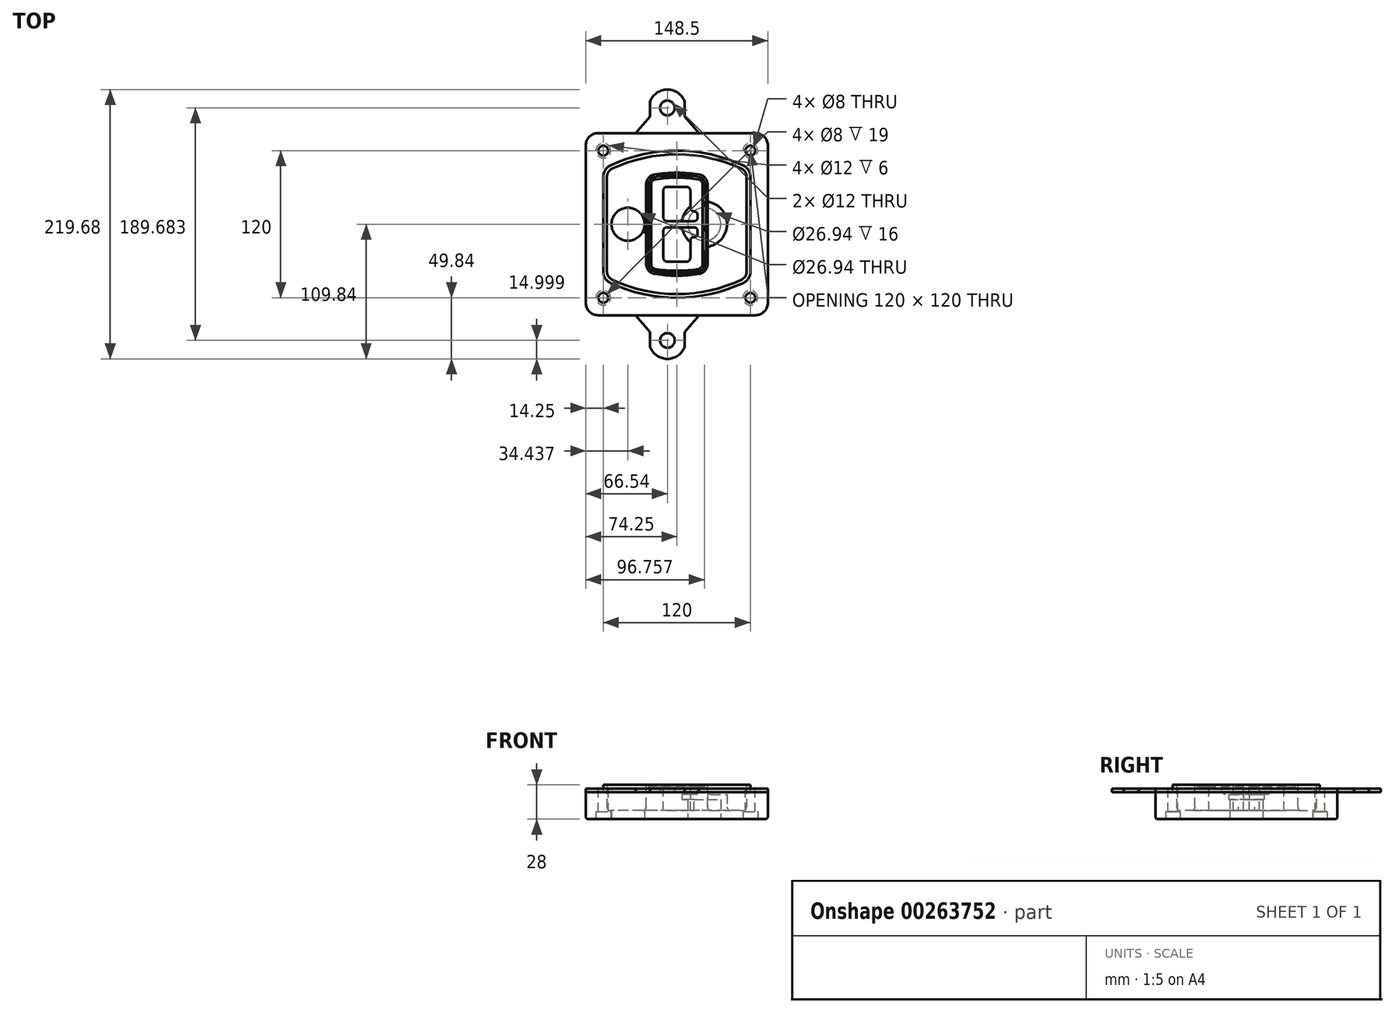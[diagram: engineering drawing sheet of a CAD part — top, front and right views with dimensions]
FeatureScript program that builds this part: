
annotation { "Feature Type Name" : "Feature", "Feature Type Description" : "" }
export const myFeature = defineFeature(function(context is Context, id is Id, definition is map)
    precondition{}
    {
        {
            var Q0;
            Q0=qCreatedBy(makeId("Top.planeOp"),FACE);
            var sketch = newSketch(context, id + "F0", { "sketchPlane" : qUnion([Q0])});
            skPoint(sketch, "E0.rect.middle", {"position": v(0, 0) * mm});
            skLineSegment(sketch, "E1.bottom", {"start": v(-64.25, -74.25) * mm, "end": v(64.25, -74.25) * mm});
            skLineSegment(sketch, "E1.top", {"start": v(-64.25, 74.25) * mm, "end": v(64.25, 74.25) * mm});
            skLineSegment(sketch, "E1.left", {"start": v(-74.25, -64.25) * mm, "end": v(-74.25, 64.25) * mm});
            skLineSegment(sketch, "E1.right", {"start": v(74.25, -64.25) * mm, "end": v(74.25, 64.25) * mm});
            skLineSegment(sketch, "E2", {"start": v(-74.25, 74.25) * mm, "end": v(74.25, -74.25) * mm, "construction": true});
            skLineSegment(sketch, "E3", {"start": v(74.25, 74.25) * mm, "end": v(-74.25, -74.25) * mm, "construction": true});
            skCircle(sketch, "E4", {"center": v(-60, 60) * mm, "radius": 4 * mm});
            skCircle(sketch, "E5", {"center": v(60, 60) * mm, "radius": 4 * mm});
            skCircle(sketch, "E6", {"center": v(60, -60) * mm, "radius": 4 * mm});
            skCircle(sketch, "E7", {"center": v(-60, -60) * mm, "radius": 4 * mm});
            skLineSegment(sketch, "E8", {"start": v(-60, 60) * mm, "end": v(60, 60) * mm, "construction": true});
            skLineSegment(sketch, "E9", {"start": v(60, 60) * mm, "end": v(60, -60) * mm, "construction": true});
            skLineSegment(sketch, "E10", {"start": v(60, -60) * mm, "end": v(-60, -60) * mm, "construction": true});
            skLineSegment(sketch, "E11", {"start": v(-60, -60) * mm, "end": v(-60, 60) * mm, "construction": true});
            skLineSegment(sketch, "E12", {"start": v(-60, 38.83) * mm, "end": v(-60, -38.83) * mm});
            skLineSegment(sketch, "E13", {"start": v(60, 38.83) * mm, "end": v(60, -38.83) * mm});
            skArc(sketch, "E14", {"start": v(54.26, 47.88) * mm, "mid": v(0, 60) * mm, "end": v(-54.26, 47.88) * mm});
            skArc(sketch, "E15", {"start": v(-54.26, -47.88) * mm, "mid": v(0, -60) * mm, "end": v(54.26, -47.88) * mm});
            skLineSegment(sketch, "E16", {"start": v(-60, 0) * mm, "end": v(60, 0) * mm, "construction": true});
            skPoint(sketch, "E17.visualSharp", {"position": v(-60, -45) * mm});
            skArc(sketch, "E17.filletArc", {"start": v(-60, -38.83) * mm, "mid": v(-58.44, -44.2) * mm, "end": v(-54.26, -47.88) * mm});
            skPoint(sketch, "E18.visualSharp", {"position": v(-60, 45) * mm});
            skArc(sketch, "E18.filletArc", {"start": v(-54.26, 47.88) * mm, "mid": v(-58.44, 44.2) * mm, "end": v(-60, 38.83) * mm});
            skPoint(sketch, "E19.visualSharp", {"position": v(60, 45) * mm});
            skArc(sketch, "E19.filletArc", {"start": v(60, 38.83) * mm, "mid": v(58.44, 44.2) * mm, "end": v(54.26, 47.88) * mm});
            skPoint(sketch, "E20.visualSharp", {"position": v(60, -45) * mm});
            skArc(sketch, "E20.filletArc", {"start": v(54.26, -47.88) * mm, "mid": v(58.44, -44.2) * mm, "end": v(60, -38.83) * mm});
            skPoint(sketch, "E21.visualSharp", {"position": v(-74.25, 74.25) * mm});
            skArc(sketch, "E21.filletArc", {"start": v(-64.25, 74.25) * mm, "mid": v(-71.32, 71.32) * mm, "end": v(-74.25, 64.25) * mm});
            skPoint(sketch, "E22.visualSharp", {"position": v(74.25, 74.25) * mm});
            skArc(sketch, "E22.filletArc", {"start": v(74.25, 64.25) * mm, "mid": v(71.32, 71.32) * mm, "end": v(64.25, 74.25) * mm});
            skPoint(sketch, "E23.visualSharp", {"position": v(74.25, -74.25) * mm});
            skArc(sketch, "E23.filletArc", {"start": v(64.25, -74.25) * mm, "mid": v(71.32, -71.32) * mm, "end": v(74.25, -64.25) * mm});
            skPoint(sketch, "E24.visualSharp", {"position": v(-74.25, -74.25) * mm});
            skArc(sketch, "E24.filletArc", {"start": v(-74.25, -64.25) * mm, "mid": v(-71.32, -71.32) * mm, "end": v(-64.25, -74.25) * mm});
            skArc(sketch, "E25.0", {"start": v(57, 38.83) * mm, "mid": v(55.9, 42.58) * mm, "end": v(52.98, 45.17) * mm});
            skLineSegment(sketch, "E25.1", {"start": v(57, 38.83) * mm, "end": v(57, -38.83) * mm});
            skArc(sketch, "E25.2", {"start": v(52.98, -45.17) * mm, "mid": v(55.9, -42.58) * mm, "end": v(57, -38.83) * mm});
            skArc(sketch, "E25.3", {"start": v(-52.98, -45.17) * mm, "mid": v(0, -57) * mm, "end": v(52.98, -45.17) * mm});
            skArc(sketch, "E25.4", {"start": v(-57, -38.83) * mm, "mid": v(-55.9, -42.58) * mm, "end": v(-52.98, -45.17) * mm});
            skArc(sketch, "E25.5", {"start": v(52.98, 45.17) * mm, "mid": v(0, 57) * mm, "end": v(-52.98, 45.17) * mm});
            skLineSegment(sketch, "E25.6", {"start": v(-57, 38.83) * mm, "end": v(-57, -38.83) * mm});
            skArc(sketch, "E25.7", {"start": v(-52.98, 45.17) * mm, "mid": v(-55.9, 42.58) * mm, "end": v(-57, 38.83) * mm});
            skArc(sketch, "E26.0", {"start": v(-55.96, 51.5) * mm, "mid": v(-61.82, 46.33) * mm, "end": v(-64, 38.83) * mm});
            skArc(sketch, "E26.1", {"start": v(55.96, 51.5) * mm, "mid": v(0, 64) * mm, "end": v(-55.96, 51.5) * mm});
            skArc(sketch, "E26.2", {"start": v(64, 38.83) * mm, "mid": v(61.82, 46.33) * mm, "end": v(55.96, 51.5) * mm});
            skLineSegment(sketch, "E26.3", {"start": v(64, 38.83) * mm, "end": v(64, -38.83) * mm});
            skArc(sketch, "E26.4", {"start": v(55.96, -51.5) * mm, "mid": v(61.82, -46.33) * mm, "end": v(64, -38.83) * mm});
            skLineSegment(sketch, "E26.5", {"start": v(-64, 38.83) * mm, "end": v(-64, -38.83) * mm});
            skArc(sketch, "E26.6", {"start": v(-55.96, -51.5) * mm, "mid": v(0, -64) * mm, "end": v(55.96, -51.5) * mm});
            skArc(sketch, "E26.7", {"start": v(-64, -38.83) * mm, "mid": v(-61.82, -46.33) * mm, "end": v(-55.96, -51.5) * mm});
            skSolve(sketch);
        }
        {
            var Q0;
            Q0=makeQuery(id+"F0.imprint","IMPRINT",FACE,{"disambiguationData":[TD([[makeQuery(id+"F0.imprint","IMPRINT",EDGE,{"derivedFrom":sQuery(id+"F0.wireOp",EDGE,"E1.bottom")}),1.0]])]});
            var Q1;
            Q1=makeQuery(id+"F0.imprint","IMPRINT",FACE,{"disambiguationData":[TD([[makeQuery(id+"F0.imprint","IMPRINT",EDGE,{"derivedFrom":sQuery(id+"F0.wireOp",EDGE,"E12")}),1.0]])]});
            var Q2;
            Q2=makeQuery(id+"F0.imprint","IMPRINT",FACE,{"disambiguationData":[TD([[makeQuery(id+"F0.imprint","IMPRINT",EDGE,{"derivedFrom":sQuery(id+"F0.wireOp",EDGE,"E25.0")}),1.0]])]});
            var Q3;
            Q3=makeQuery(id+"F0.imprint","IMPRINT",FACE,{"disambiguationData":[TD([[makeQuery(id+"F0.imprint","IMPRINT",EDGE,{"derivedFrom":sQuery(id+"F0.wireOp",EDGE,"E12")}),-1.0]])]});
            extrude(context, id + "F1", {"entities" : qUnion([Q0, Q1, Q2, Q3]), "oppositeDirection" : true, "depth" : 25 * mm});
        }
        {
            var Q0;
            Q0=makeQuery(id+"F0.imprint","IMPRINT",FACE,{"disambiguationData":[TD([[makeQuery(id+"F0.imprint","IMPRINT",EDGE,{"derivedFrom":sQuery(id+"F0.wireOp",EDGE,"E12")}),1.0]])]});
            extrude(context, id + "F2", {"entities" : qUnion([Q0]), "operationType" : NewBodyOperationType.ADD, "depth" : 3 * mm});
        }
        {
            var Q0;
            Q0=makeQuery(id+"F0.imprint","IMPRINT",FACE,{"disambiguationData":[TD([[makeQuery(id+"F0.imprint","IMPRINT",EDGE,{"derivedFrom":sQuery(id+"F0.wireOp",EDGE,"E25.0")}),1.0]])]});
            extrude(context, id + "F3", {"entities" : qUnion([Q0]), "operationType" : NewBodyOperationType.REMOVE, "oppositeDirection" : true, "depth" : 18 * mm});
        }
        {
            var Q0;
            Q0=makeQuery(id+"F2.opExtrude","CAP_FACE",FACE,{"disambiguationData":[OSD([sQuery(id+"F0.wireOp",EDGE,"E12"),sQuery(id+"F0.wireOp",EDGE,"E13"),sQuery(id+"F0.wireOp",EDGE,"E14"),sQuery(id+"F0.wireOp",EDGE,"E15"),sQuery(id+"F0.wireOp",EDGE,"E17.filletArc"),sQuery(id+"F0.wireOp",EDGE,"E18.filletArc"),sQuery(id+"F0.wireOp",EDGE,"E19.filletArc"),sQuery(id+"F0.wireOp",EDGE,"E20.filletArc"),sQuery(id+"F0.wireOp",EDGE,"E25.0"),sQuery(id+"F0.wireOp",EDGE,"E25.1"),sQuery(id+"F0.wireOp",EDGE,"E25.2"),sQuery(id+"F0.wireOp",EDGE,"E25.3"),sQuery(id+"F0.wireOp",EDGE,"E25.4"),sQuery(id+"F0.wireOp",EDGE,"E25.5"),sQuery(id+"F0.wireOp",EDGE,"E25.6"),sQuery(id+"F0.wireOp",EDGE,"E25.7")])],"isStart":false});
            var sketch = newSketch(context, id + "F4", { "sketchPlane" : qUnion([Q0])});
            skArc(sketch, "E27.0", {"start": v(-18.34, -40.45) * mm, "mid": v(0, -42) * mm, "end": v(18.34, -40.45) * mm});
            skArc(sketch, "E28.0", {"start": v(18.34, 40.45) * mm, "mid": v(0, 42) * mm, "end": v(-18.34, 40.45) * mm});
            skLineSegment(sketch, "E29", {"start": v(-25, 32.57) * mm, "end": v(-25, -32.57) * mm});
            skLineSegment(sketch, "E30", {"start": v(25, 32.57) * mm, "end": v(25, -32.57) * mm});
            skLineSegment(sketch, "E31", {"start": v(-25, 39.1) * mm, "end": v(25, 39.1) * mm, "construction": true});
            skLineSegment(sketch, "E32", {"start": v(-25, -39.1) * mm, "end": v(25, -39.1) * mm, "construction": true});
            skPoint(sketch, "E33.visualSharp", {"position": v(-25, 39.1) * mm});
            skArc(sketch, "E33.filletArc", {"start": v(-18.34, 40.45) * mm, "mid": v(-23.11, 37.73) * mm, "end": v(-25, 32.57) * mm});
            skPoint(sketch, "E34.visualSharp", {"position": v(25, 39.1) * mm});
            skArc(sketch, "E34.filletArc", {"start": v(25, 32.57) * mm, "mid": v(23.11, 37.73) * mm, "end": v(18.34, 40.45) * mm});
            skPoint(sketch, "E35.visualSharp", {"position": v(25, -39.1) * mm});
            skArc(sketch, "E35.filletArc", {"start": v(18.34, -40.45) * mm, "mid": v(23.11, -37.73) * mm, "end": v(25, -32.57) * mm});
            skPoint(sketch, "E36.visualSharp", {"position": v(-25, -39.1) * mm});
            skArc(sketch, "E36.filletArc", {"start": v(-25, -32.57) * mm, "mid": v(-23.11, -37.73) * mm, "end": v(-18.34, -40.45) * mm});
            skArc(sketch, "E37.0", {"start": v(52.98, 45.17) * mm, "mid": v(0, 57) * mm, "end": v(-52.98, 45.17) * mm});
            skArc(sketch, "E37.1", {"start": v(-52.98, 45.17) * mm, "mid": v(-55.9, 42.58) * mm, "end": v(-57, 38.83) * mm});
            skLineSegment(sketch, "E37.2", {"start": v(-57, 38.83) * mm, "end": v(-57, -38.83) * mm});
            skArc(sketch, "E37.3", {"start": v(-57, -38.83) * mm, "mid": v(-55.9, -42.58) * mm, "end": v(-52.98, -45.17) * mm});
            skArc(sketch, "E37.4", {"start": v(-52.98, -45.17) * mm, "mid": v(0, -57) * mm, "end": v(52.98, -45.17) * mm});
            skArc(sketch, "E37.5", {"start": v(52.98, -45.17) * mm, "mid": v(55.9, -42.58) * mm, "end": v(57, -38.83) * mm});
            skLineSegment(sketch, "E37.6", {"start": v(57, 38.83) * mm, "end": v(57, -38.83) * mm});
            skArc(sketch, "E37.7", {"start": v(57, 38.83) * mm, "mid": v(55.9, 42.58) * mm, "end": v(52.98, 45.17) * mm});
            skLineSegment(sketch, "E38.0", {"start": v(23, 32.57) * mm, "end": v(23, -32.57) * mm});
            skArc(sketch, "E38.1", {"start": v(18, -38.48) * mm, "mid": v(21.58, -36.44) * mm, "end": v(23, -32.57) * mm});
            skArc(sketch, "E38.2", {"start": v(-18, -38.48) * mm, "mid": v(0, -40) * mm, "end": v(18, -38.48) * mm});
            skArc(sketch, "E38.3", {"start": v(-23, -32.57) * mm, "mid": v(-21.58, -36.44) * mm, "end": v(-18, -38.48) * mm});
            skLineSegment(sketch, "E38.4", {"start": v(-23, 32.57) * mm, "end": v(-23, -32.57) * mm});
            skArc(sketch, "E38.5", {"start": v(23, 32.57) * mm, "mid": v(21.58, 36.44) * mm, "end": v(18, 38.48) * mm});
            skArc(sketch, "E38.6", {"start": v(-18, 38.48) * mm, "mid": v(-21.58, 36.44) * mm, "end": v(-23, 32.57) * mm});
            skArc(sketch, "E38.7", {"start": v(18, 38.48) * mm, "mid": v(0, 40) * mm, "end": v(-18, 38.48) * mm});
            skArc(sketch, "E39.0", {"start": v(21, 32.57) * mm, "mid": v(20.06, 35.15) * mm, "end": v(17.67, 36.5) * mm});
            skLineSegment(sketch, "E39.1", {"start": v(21, 32.57) * mm, "end": v(21, -32.57) * mm});
            skArc(sketch, "E39.2", {"start": v(17.67, -36.5) * mm, "mid": v(20.06, -35.15) * mm, "end": v(21, -32.57) * mm});
            skArc(sketch, "E39.3", {"start": v(-17.67, -36.5) * mm, "mid": v(0, -38) * mm, "end": v(17.67, -36.5) * mm});
            skArc(sketch, "E39.4", {"start": v(-21, -32.57) * mm, "mid": v(-20.06, -35.15) * mm, "end": v(-17.67, -36.5) * mm});
            skArc(sketch, "E39.5", {"start": v(17.67, 36.5) * mm, "mid": v(0, 38) * mm, "end": v(-17.67, 36.5) * mm});
            skLineSegment(sketch, "E39.6", {"start": v(-21, 32.57) * mm, "end": v(-21, -32.57) * mm});
            skArc(sketch, "E39.7", {"start": v(-17.67, 36.5) * mm, "mid": v(-20.06, 35.15) * mm, "end": v(-21, 32.57) * mm});
            skLineSegment(sketch, "E40", {"start": v(-25, 0) * mm, "end": v(25, 0) * mm, "construction": true});
            skLineSegment(sketch, "E41", {"start": v(-11, 5.5) * mm, "end": v(-11, 27.5) * mm});
            skLineSegment(sketch, "E42", {"start": v(-8, 30.5) * mm, "end": v(8, 30.5) * mm});
            skLineSegment(sketch, "E43", {"start": v(11, 27.5) * mm, "end": v(11, 13.5) * mm});
            skLineSegment(sketch, "E44", {"start": v(14, 10.5) * mm, "end": v(14, 10.5) * mm});
            skLineSegment(sketch, "E45", {"start": v(17, 7.5) * mm, "end": v(17, 5.5) * mm});
            skLineSegment(sketch, "E46", {"start": v(14, 2.5) * mm, "end": v(-8, 2.5) * mm});
            skPoint(sketch, "E47.visualSharp", {"position": v(-11, 30.5) * mm});
            skArc(sketch, "E47.filletArc", {"start": v(-8, 30.5) * mm, "mid": v(-10.12, 29.62) * mm, "end": v(-11, 27.5) * mm});
            skPoint(sketch, "E48.visualSharp", {"position": v(11, 30.5) * mm});
            skArc(sketch, "E48.filletArc", {"start": v(11, 27.5) * mm, "mid": v(10.12, 29.62) * mm, "end": v(8, 30.5) * mm});
            skPoint(sketch, "E49.visualSharp", {"position": v(11, 10.5) * mm});
            skArc(sketch, "E49.filletArc", {"start": v(11, 13.5) * mm, "mid": v(11.88, 11.38) * mm, "end": v(14, 10.5) * mm});
            skPoint(sketch, "E50.visualSharp", {"position": v(17, 10.5) * mm});
            skArc(sketch, "E50.filletArc", {"start": v(17, 7.5) * mm, "mid": v(16.12, 9.62) * mm, "end": v(14, 10.5) * mm});
            skPoint(sketch, "E51.visualSharp", {"position": v(17, 2.5) * mm});
            skArc(sketch, "E51.filletArc", {"start": v(14, 2.5) * mm, "mid": v(16.12, 3.38) * mm, "end": v(17, 5.5) * mm});
            skPoint(sketch, "E52.visualSharp", {"position": v(-11, 2.5) * mm});
            skArc(sketch, "E52.filletArc", {"start": v(-11, 5.5) * mm, "mid": v(-10.12, 3.38) * mm, "end": v(-8, 2.5) * mm});
            skLineSegment(sketch, "E53.0.MirrorCS", {"start": v(14, -2.5) * mm, "end": v(-8, -2.5) * mm});
            skArc(sketch, "E54.0.MirrorCS", {"start": v(-11, -5.5) * mm, "mid": v(-10.12, -3.38) * mm, "end": v(-8, -2.5) * mm});
            skLineSegment(sketch, "E55.0.MirrorCS", {"start": v(-11, -5.5) * mm, "end": v(-11, -27.5) * mm});
            skArc(sketch, "E56.0.MirrorCS", {"start": v(-8, -30.5) * mm, "mid": v(-10.12, -29.62) * mm, "end": v(-11, -27.5) * mm});
            skLineSegment(sketch, "E57.0.MirrorCS", {"start": v(-8, -30.5) * mm, "end": v(8, -30.5) * mm});
            skArc(sketch, "E58.0.MirrorCS", {"start": v(11, -27.5) * mm, "mid": v(10.12, -29.62) * mm, "end": v(8, -30.5) * mm});
            skLineSegment(sketch, "E59.0.MirrorCS", {"start": v(11, -27.5) * mm, "end": v(11, -13.5) * mm});
            skArc(sketch, "E60.0.MirrorCS", {"start": v(11, -13.5) * mm, "mid": v(11.88, -11.38) * mm, "end": v(14, -10.5) * mm});
            skArc(sketch, "E61.0.MirrorCS", {"start": v(17, -7.5) * mm, "mid": v(16.12, -9.62) * mm, "end": v(14, -10.5) * mm});
            skLineSegment(sketch, "E62.0.MirrorCS", {"start": v(17, -7.5) * mm, "end": v(17, -5.5) * mm});
            skArc(sketch, "E63.0.MirrorCS", {"start": v(14, -2.5) * mm, "mid": v(16.12, -3.38) * mm, "end": v(17, -5.5) * mm});
            skSolve(sketch);
        }
        {
            var Q0;
            Q0=makeQuery(id+"F4.imprint","IMPRINT",FACE,{"disambiguationData":[TD([[makeQuery(id+"F4.imprint","IMPRINT",EDGE,{"derivedFrom":sQuery(id+"F4.wireOp",EDGE,"E27.0")}),1.0]])]});
            var Q1;
            Q1=makeQuery(id+"F4.imprint","IMPRINT",FACE,{"disambiguationData":[TD([[makeQuery(id+"F4.imprint","IMPRINT",EDGE,{"derivedFrom":sQuery(id+"F4.wireOp",EDGE,"E38.0")}),-1.0]])]});
            var Q2;
            Q2=makeQuery(id+"F4.imprint","IMPRINT",FACE,{"disambiguationData":[TD([[makeQuery(id+"F4.imprint","IMPRINT",EDGE,{"derivedFrom":sQuery(id+"F4.wireOp",EDGE,"E39.0")}),1.0]])]});
            extrude(context, id + "F5", {"entities" : qUnion([Q0, Q1, Q2]), "operationType" : NewBodyOperationType.ADD, "endBound" : BoundingType.UP_TO_NEXT, "oppositeDirection" : true, "depth" : 25 * mm});
        }
        {
            var Q0;
            Q0=makeQuery(id+"F4.imprint","IMPRINT",FACE,{"disambiguationData":[TD([[makeQuery(id+"F4.imprint","IMPRINT",EDGE,{"derivedFrom":sQuery(id+"F4.wireOp",EDGE,"E38.0")}),-1.0]])]});
            extrude(context, id + "F6", {"entities" : qUnion([Q0]), "operationType" : NewBodyOperationType.REMOVE, "oppositeDirection" : true, "depth" : 2 * mm});
        }
        {
            var Q0;
            Q0=makeQuery(id+"F1.opExtrude","CAP_FACE",FACE,{"disambiguationData":[OSD([sQuery(id+"F0.wireOp",EDGE,"E1.bottom"),sQuery(id+"F0.wireOp",EDGE,"E1.top"),sQuery(id+"F0.wireOp",EDGE,"E1.left"),sQuery(id+"F0.wireOp",EDGE,"E1.right"),sQuery(id+"F0.wireOp",EDGE,"E4"),sQuery(id+"F0.wireOp",EDGE,"E5"),sQuery(id+"F0.wireOp",EDGE,"E6"),sQuery(id+"F0.wireOp",EDGE,"E7"),sQuery(id+"F0.wireOp",EDGE,"E21.filletArc"),sQuery(id+"F0.wireOp",EDGE,"E22.filletArc"),sQuery(id+"F0.wireOp",EDGE,"E23.filletArc"),sQuery(id+"F0.wireOp",EDGE,"E24.filletArc")])],"isStart":false});
            var sketch = newSketch(context, id + "F7", { "sketchPlane" : qUnion([Q0])});
            skCircle(sketch, "E64", {"center": v(22.5, 0) * mm, "radius": 13.47 * mm});
            skCircle(sketch, "E65", {"center": v(-39.81, 0) * mm, "radius": 13.47 * mm});
            skLineSegment(sketch, "E66", {"start": v(74.25, 0) * mm, "end": v(-74.25, 0) * mm});
            skCircle(sketch, "E67", {"center": v(22.5, 0) * mm, "radius": 18.47 * mm});
            skCircle(sketch, "E68", {"center": v(60, -60) * mm, "radius": 6 * mm});
            skCircle(sketch, "E69", {"center": v(-60, -60) * mm, "radius": 6 * mm});
            skCircle(sketch, "E70", {"center": v(-60, 60) * mm, "radius": 6 * mm});
            skCircle(sketch, "E71", {"center": v(60, 60) * mm, "radius": 6 * mm});
            skSolve(sketch);
        }
        {
            var Q0;
            {var subQ1=sQuery(id+"F7.wireOp",EDGE,"E66");var subQ4=sQuery(id+"F7.wireOp",EDGE,"E64");var subQ6=makeQuery(id+"F7.imprint","INTERSECT",VERTEX,{"disambiguationData":[OD(0.0)],"derivedFrom":[subQ4,subQ1]});Q0=makeQuery(id+"F7.imprint","IMPRINT",FACE,{"disambiguationData":[TD([[makeQuery(id+"F7.imprint","IMPRINT",EDGE,{"disambiguationData":[TD([[subQ6,-1.0]])],"derivedFrom":subQ4}),-1.0]])]});}
            var Q1;
            {var subQ0=sQuery(id+"F7.wireOp",EDGE,"E66");var subQ1=sQuery(id+"F7.wireOp",EDGE,"E64");var subQ3=makeQuery(id+"F7.imprint","INTERSECT",VERTEX,{"disambiguationData":[OD(0.0)],"derivedFrom":[subQ1,subQ0]});Q1=makeQuery(id+"F7.imprint","IMPRINT",FACE,{"disambiguationData":[TD([[makeQuery(id+"F7.imprint","IMPRINT",EDGE,{"disambiguationData":[TD([[subQ3,-1.0]])],"derivedFrom":subQ1}),1.0]])]});}
            var Q2;
            {var subQ0=sQuery(id+"F7.wireOp",EDGE,"E66");var subQ1=sQuery(id+"F7.wireOp",EDGE,"E64");var subQ3=makeQuery(id+"F7.imprint","INTERSECT",VERTEX,{"disambiguationData":[OD(0.0)],"derivedFrom":[subQ1,subQ0]});Q2=makeQuery(id+"F7.imprint","IMPRINT",FACE,{"disambiguationData":[TD([[makeQuery(id+"F7.imprint","IMPRINT",EDGE,{"disambiguationData":[TD([[subQ3,1.0]])],"derivedFrom":subQ1}),1.0]])]});}
            var Q3;
            {var subQ1=sQuery(id+"F7.wireOp",EDGE,"E66");var subQ4=sQuery(id+"F7.wireOp",EDGE,"E64");var subQ6=makeQuery(id+"F7.imprint","INTERSECT",VERTEX,{"disambiguationData":[OD(0.0)],"derivedFrom":[subQ4,subQ1]});Q3=makeQuery(id+"F7.imprint","IMPRINT",FACE,{"disambiguationData":[TD([[makeQuery(id+"F7.imprint","IMPRINT",EDGE,{"disambiguationData":[TD([[subQ6,1.0]])],"derivedFrom":subQ4}),-1.0]])]});}
            extrude(context, id + "F8", {"entities" : qUnion([Q0, Q1, Q2, Q3]), "operationType" : NewBodyOperationType.ADD, "oppositeDirection" : true, "depth" : 20 * mm});
        }
        {
            var Q0;
            {var subQ0=sQuery(id+"F7.wireOp",EDGE,"E66");var subQ1=sQuery(id+"F7.wireOp",EDGE,"E64");var subQ3=makeQuery(id+"F7.imprint","INTERSECT",VERTEX,{"disambiguationData":[OD(0.0)],"derivedFrom":[subQ1,subQ0]});Q0=makeQuery(id+"F7.imprint","IMPRINT",FACE,{"disambiguationData":[TD([[makeQuery(id+"F7.imprint","IMPRINT",EDGE,{"disambiguationData":[TD([[subQ3,-1.0]])],"derivedFrom":subQ1}),1.0]])]});}
            var Q1;
            {var subQ0=sQuery(id+"F7.wireOp",EDGE,"E66");var subQ1=sQuery(id+"F7.wireOp",EDGE,"E64");var subQ3=makeQuery(id+"F7.imprint","INTERSECT",VERTEX,{"disambiguationData":[OD(0.0)],"derivedFrom":[subQ1,subQ0]});Q1=makeQuery(id+"F7.imprint","IMPRINT",FACE,{"disambiguationData":[TD([[makeQuery(id+"F7.imprint","IMPRINT",EDGE,{"disambiguationData":[TD([[subQ3,1.0]])],"derivedFrom":subQ1}),1.0]])]});}
            extrude(context, id + "F9", {"entities" : qUnion([Q0, Q1]), "operationType" : NewBodyOperationType.REMOVE, "oppositeDirection" : true, "depth" : 16 * mm});
        }
        {
            var Q0;
            {var subQ0=sQuery(id+"F7.wireOp",EDGE,"E66");var subQ1=sQuery(id+"F7.wireOp",EDGE,"E65");var subQ3=makeQuery(id+"F7.imprint","INTERSECT",VERTEX,{"disambiguationData":[OD(0.0)],"derivedFrom":[subQ1,subQ0]});Q0=makeQuery(id+"F7.imprint","IMPRINT",FACE,{"disambiguationData":[TD([[makeQuery(id+"F7.imprint","IMPRINT",EDGE,{"disambiguationData":[TD([[subQ3,-1.0]])],"derivedFrom":subQ1}),1.0]])]});}
            var Q1;
            {var subQ0=sQuery(id+"F7.wireOp",EDGE,"E66");var subQ1=sQuery(id+"F7.wireOp",EDGE,"E65");var subQ3=makeQuery(id+"F7.imprint","INTERSECT",VERTEX,{"disambiguationData":[OD(0.0)],"derivedFrom":[subQ1,subQ0]});Q1=makeQuery(id+"F7.imprint","IMPRINT",FACE,{"disambiguationData":[TD([[makeQuery(id+"F7.imprint","IMPRINT",EDGE,{"disambiguationData":[TD([[subQ3,1.0]])],"derivedFrom":subQ1}),1.0]])]});}
            extrude(context, id + "F10", {"entities" : qUnion([Q0, Q1]), "operationType" : NewBodyOperationType.REMOVE, "oppositeDirection" : true, "depth" : 25 * mm});
        }
        {
            var Q0;
            Q0=makeQuery(id+"F7.imprint","IMPRINT",FACE,{"disambiguationData":[TD([[makeQuery(id+"F7.imprint","IMPRINT",EDGE,{"derivedFrom":sQuery(id+"F7.wireOp",EDGE,"E68")}),1.0]])]});
            var Q1;
            Q1=makeQuery(id+"F7.imprint","IMPRINT",FACE,{"disambiguationData":[TD([[makeQuery(id+"F7.imprint","IMPRINT",EDGE,{"derivedFrom":makeQuery(id+"F1.opExtrude","CAP_EDGE",EDGE,{"disambiguationData":[OSD([sQuery(id+"F0.wireOp",EDGE,"E5")])],"isStart":false})}),-1.0]])]});
            var Q2;
            Q2=makeQuery(id+"F7.imprint","IMPRINT",FACE,{"disambiguationData":[TD([[makeQuery(id+"F7.imprint","IMPRINT",EDGE,{"derivedFrom":sQuery(id+"F7.wireOp",EDGE,"E69")}),1.0]])]});
            var Q3;
            Q3=makeQuery(id+"F7.imprint","IMPRINT",FACE,{"disambiguationData":[TD([[makeQuery(id+"F7.imprint","IMPRINT",EDGE,{"derivedFrom":makeQuery(id+"F1.opExtrude","CAP_EDGE",EDGE,{"disambiguationData":[OSD([sQuery(id+"F0.wireOp",EDGE,"E4")])],"isStart":false})}),-1.0]])]});
            var Q4;
            Q4=makeQuery(id+"F7.imprint","IMPRINT",FACE,{"disambiguationData":[TD([[makeQuery(id+"F7.imprint","IMPRINT",EDGE,{"derivedFrom":sQuery(id+"F7.wireOp",EDGE,"E70")}),1.0]])]});
            var Q5;
            Q5=makeQuery(id+"F7.imprint","IMPRINT",FACE,{"disambiguationData":[TD([[makeQuery(id+"F7.imprint","IMPRINT",EDGE,{"derivedFrom":makeQuery(id+"F1.opExtrude","CAP_EDGE",EDGE,{"disambiguationData":[OSD([sQuery(id+"F0.wireOp",EDGE,"E7")])],"isStart":false})}),-1.0]])]});
            var Q6;
            Q6=makeQuery(id+"F7.imprint","IMPRINT",FACE,{"disambiguationData":[TD([[makeQuery(id+"F7.imprint","IMPRINT",EDGE,{"derivedFrom":sQuery(id+"F7.wireOp",EDGE,"E71")}),1.0]])]});
            var Q7;
            Q7=makeQuery(id+"F7.imprint","IMPRINT",FACE,{"disambiguationData":[TD([[makeQuery(id+"F7.imprint","IMPRINT",EDGE,{"derivedFrom":makeQuery(id+"F1.opExtrude","CAP_EDGE",EDGE,{"disambiguationData":[OSD([sQuery(id+"F0.wireOp",EDGE,"E6")])],"isStart":false})}),-1.0]])]});
            extrude(context, id + "F11", {"entities" : qUnion([Q0, Q1, Q2, Q3, Q4, Q5, Q6, Q7]), "operationType" : NewBodyOperationType.REMOVE, "oppositeDirection" : true, "depth" : 6 * mm});
        }
        {
            var Q0;
            Q0=makeQuery(id+"F9.boolean.opBoolean","COPY",FACE,{"derivedFrom":makeQuery(id+"F9.opExtrude","CAP_FACE",FACE,{"disambiguationData":[OSD([sQuery(id+"F7.wireOp",EDGE,"E64")])],"isStart":false})});
            var sketch = newSketch(context, id + "F12", { "sketchPlane" : qUnion([Q0])});
            skArc(sketch, "E72.0", {"start": v(11, 14.45) * mm, "mid": v(6.45, 9.13) * mm, "end": v(4.2, 2.5) * mm});
            skArc(sketch, "E72.1", {"start": v(4.2, -2.5) * mm, "mid": v(6.45, -9.13) * mm, "end": v(11, -14.45) * mm});
            skLineSegment(sketch, "E73", {"start": v(4.2, -2.5) * mm, "end": v(14, -2.5) * mm});
            skLineSegment(sketch, "E74.0", {"start": v(14, 2.5) * mm, "end": v(4.2, 2.5) * mm});
            skArc(sketch, "E74.1", {"start": v(14, 2.5) * mm, "mid": v(16.12, 3.38) * mm, "end": v(17, 5.5) * mm});
            skLineSegment(sketch, "E74.2", {"start": v(17, 7.5) * mm, "end": v(17, 5.5) * mm});
            skArc(sketch, "E74.3", {"start": v(17, 7.5) * mm, "mid": v(16.12, 9.62) * mm, "end": v(14, 10.5) * mm});
            skArc(sketch, "E74.4", {"start": v(11, 13.5) * mm, "mid": v(11.88, 11.38) * mm, "end": v(14, 10.5) * mm});
            skLineSegment(sketch, "E74.5", {"start": v(11, 14.45) * mm, "end": v(11, 13.5) * mm});
            skLineSegment(sketch, "E74.7", {"start": v(14, -2.5) * mm, "end": v(4.2, -2.5) * mm});
            skArc(sketch, "E74.8", {"start": v(14, -2.5) * mm, "mid": v(16.12, -3.38) * mm, "end": v(17, -5.5) * mm});
            skLineSegment(sketch, "E74.9", {"start": v(17, -7.5) * mm, "end": v(17, -5.5) * mm});
            skArc(sketch, "E74.10", {"start": v(17, -7.5) * mm, "mid": v(16.12, -9.62) * mm, "end": v(14, -10.5) * mm});
            skArc(sketch, "E74.11", {"start": v(11, -13.5) * mm, "mid": v(11.88, -11.38) * mm, "end": v(14, -10.5) * mm});
            skLineSegment(sketch, "E74.12", {"start": v(11, -14.45) * mm, "end": v(11, -13.5) * mm});
            skPoint(sketch, "E75.orphan", {"position": v(11, -27.5) * mm});
            skPoint(sketch, "E76.orphan", {"position": v(-8, -2.5) * mm});
            skPoint(sketch, "E77.orphan", {"position": v(-8, 2.5) * mm});
            skPoint(sketch, "E78.orphan", {"position": v(11, 27.5) * mm});
            skSolve(sketch);
        }
        {
            var Q0;
            {var subQ7=sQuery(id+"F12.wireOp",EDGE,"E72.0");var subQ14=sQuery(id+"F12.wireOp",EDGE,"E72.1");var subQ16=sQuery(id+"F12.wireOp",EDGE,"E74.1");var subQ18=sQuery(id+"F12.wireOp",EDGE,"E74.8");Q0=qUnion([makeQuery(id+"F12.imprint","IMPRINT",FACE,{"disambiguationData":[TD([[makeQuery(id+"F12.imprint","IMPRINT",EDGE,{"derivedFrom":subQ7}),1.0]])]}),makeQuery(id+"F12.imprint","IMPRINT",FACE,{"disambiguationData":[TD([[makeQuery(id+"F12.imprint","IMPRINT",EDGE,{"derivedFrom":subQ14}),1.0]])]}),makeQuery(id+"F12.imprint","IMPRINT",FACE,{"disambiguationData":[TD([[makeQuery(id+"F12.imprint","IMPRINT",EDGE,{"derivedFrom":subQ16}),1.0]])]}),makeQuery(id+"F12.imprint","IMPRINT",FACE,{"disambiguationData":[TD([[makeQuery(id+"F12.imprint","IMPRINT",EDGE,{"derivedFrom":subQ18}),-1.0]])]})]);}
            var Q1;
            Q1=makeQuery(id+"F5.boolean.opBoolean","SPLIT",FACE,{"disambiguationData":[TD([makeQuery(id+"F5.opExtrude","SWEPT_FACE",FACE,{"disambiguationData":[OSD([sQuery(id+"F4.wireOp",EDGE,"E41")])]})])],"derivedFrom":makeQuery(id+"F3.boolean.opBoolean","COPY",FACE,{"derivedFrom":makeQuery(id+"F3.opExtrude","CAP_FACE",FACE,{"disambiguationData":[OSD([sQuery(id+"F0.wireOp",EDGE,"E25.0"),sQuery(id+"F0.wireOp",EDGE,"E25.1"),sQuery(id+"F0.wireOp",EDGE,"E25.2"),sQuery(id+"F0.wireOp",EDGE,"E25.3"),sQuery(id+"F0.wireOp",EDGE,"E25.4"),sQuery(id+"F0.wireOp",EDGE,"E25.5"),sQuery(id+"F0.wireOp",EDGE,"E25.6"),sQuery(id+"F0.wireOp",EDGE,"E25.7")])],"isStart":false})})});
            extrude(context, id + "F13", {"entities" : qUnion([Q0]), "operationType" : NewBodyOperationType.REMOVE, "endBound" : BoundingType.UP_TO_SURFACE, "endBoundEntityFace" : qUnion([Q1]), "depth" : 25 * mm});
        }
        {
            var Q0;
            Q0=makeQuery(id+"F3.boolean.opBoolean","COPY",EDGE,{"derivedFrom":makeQuery(id+"F3.opExtrude","CAP_EDGE",EDGE,{"disambiguationData":[OSD([sQuery(id+"F0.wireOp",EDGE,"E25.6")])],"isStart":false})});
            var Q1;
            Q1=makeQuery(id+"F8.boolean.opBoolean","INTERSECT",EDGE,{"derivedFrom":[makeQuery(id+"F5.opExtrude","SWEPT_FACE",FACE,{"disambiguationData":[OSD([sQuery(id+"F4.wireOp",EDGE,"E30")])]}),makeQuery(id+"F8.opExtrude","CAP_FACE",FACE,{"disambiguationData":[OSD([sQuery(id+"F7.wireOp",EDGE,"E67")])],"isStart":false})]});
            var Q2;
            Q2=makeQuery(id+"F8.boolean.opBoolean","INTERSECT",EDGE,{"disambiguationData":[OD(1.0)],"derivedFrom":[makeQuery(id+"F5.opExtrude","SWEPT_FACE",FACE,{"disambiguationData":[OSD([sQuery(id+"F4.wireOp",EDGE,"E30")])]}),makeQuery(id+"F8.opExtrude","SWEPT_FACE",FACE,{"disambiguationData":[OSD([sQuery(id+"F7.wireOp",EDGE,"E67")])]})]});
            var Q3;
            {var subQ0=sQuery(id+"F4.wireOp",EDGE,"E30");Q3=makeQuery(id+"F8.boolean.opBoolean","SPLIT",EDGE,{"disambiguationData":[TD([makeQuery(id+"F5.opExtrude","SWEPT_FACE",FACE,{"disambiguationData":[OSD([sQuery(id+"F4.wireOp",EDGE,"E35.filletArc")])]})])],"derivedFrom":makeQuery(id+"F5.opExtrude","CAP_EDGE",EDGE,{"disambiguationData":[OSD([subQ0])],"isStart":false})});}
            var Q4;
            {var subQ0=sQuery(id+"F0.wireOp",EDGE,"E25.7");var subQ1=sQuery(id+"F0.wireOp",EDGE,"E25.1");var subQ2=sQuery(id+"F0.wireOp",EDGE,"E25.6");var subQ3=sQuery(id+"F0.wireOp",EDGE,"E25.5");var subQ4=sQuery(id+"F0.wireOp",EDGE,"E25.4");var subQ5=sQuery(id+"F0.wireOp",EDGE,"E25.0");var subQ6=sQuery(id+"F0.wireOp",EDGE,"E25.2");var subQ7=sQuery(id+"F0.wireOp",EDGE,"E25.3");Q4=makeQuery(id+"F8.boolean.opBoolean","INTERSECT",EDGE,{"derivedFrom":[makeQuery(id+"F5.boolean.opBoolean","SPLIT",FACE,{"disambiguationData":[TD([makeQuery(id+"F2.opExtrude","SWEPT_FACE",FACE,{"disambiguationData":[OSD([subQ5])]})])],"derivedFrom":makeQuery(id+"F3.boolean.opBoolean","COPY",FACE,{"derivedFrom":makeQuery(id+"F3.opExtrude","CAP_FACE",FACE,{"disambiguationData":[OSD([subQ5,subQ1,subQ6,subQ7,subQ4,subQ3,subQ2,subQ0])],"isStart":false})})}),makeQuery(id+"F8.opExtrude","SWEPT_FACE",FACE,{"disambiguationData":[OSD([sQuery(id+"F7.wireOp",EDGE,"E67")])]})]});}
            var Q5;
            Q5=makeQuery(id+"F8.boolean.opBoolean","INTERSECT",EDGE,{"disambiguationData":[OD(0.0)],"derivedFrom":[makeQuery(id+"F5.opExtrude","SWEPT_FACE",FACE,{"disambiguationData":[OSD([sQuery(id+"F4.wireOp",EDGE,"E30")])]}),makeQuery(id+"F8.opExtrude","SWEPT_FACE",FACE,{"disambiguationData":[OSD([sQuery(id+"F7.wireOp",EDGE,"E67")])]})]});
            fillet(context, id + "F14", {"entities" : qUnion([Q0, Q1, Q2, Q3, Q4, Q5]), "radius" : 3 * mm, "tangentPropagation" : true, "allowEdgeOverflow" : false});
        }
        {
            var Q0;
            Q0=makeQuery(id+"F1.opExtrude","CAP_EDGE",EDGE,{"disambiguationData":[OSD([sQuery(id+"F0.wireOp",EDGE,"E1.bottom")])],"isStart":false});
            fillet(context, id + "F15", {"entities" : qUnion([Q0]), "radius" : 2 * mm, "tangentPropagation" : true, "allowEdgeOverflow" : false});
        }
        {
            var Q0;
            {var subQ0=sQuery(id+"F0.wireOp",EDGE,"E22.filletArc");var subQ1=sQuery(id+"F0.wireOp",EDGE,"E7");var subQ2=sQuery(id+"F0.wireOp",EDGE,"E6");var subQ3=sQuery(id+"F0.wireOp",EDGE,"E5");var subQ4=sQuery(id+"F0.wireOp",EDGE,"E4");var subQ5=sQuery(id+"F0.wireOp",EDGE,"E1.bottom");var subQ6=sQuery(id+"F0.wireOp",EDGE,"E21.filletArc");var subQ7=sQuery(id+"F0.wireOp",EDGE,"E1.top");var subQ8=sQuery(id+"F0.wireOp",EDGE,"E1.left");var subQ9=sQuery(id+"F0.wireOp",EDGE,"E1.right");var subQ10=sQuery(id+"F0.wireOp",EDGE,"E23.filletArc");var subQ11=sQuery(id+"F0.wireOp",EDGE,"E24.filletArc");Q0=makeQuery(id+"F2.boolean.opBoolean","SPLIT",FACE,{"disambiguationData":[TD([makeQuery(id+"F1.opExtrude","SWEPT_FACE",FACE,{"disambiguationData":[OSD([subQ5])]})])],"derivedFrom":makeQuery(id+"F1.opExtrude","CAP_FACE",FACE,{"disambiguationData":[OSD([subQ5,subQ7,subQ8,subQ9,subQ4,subQ3,subQ2,subQ1,subQ6,subQ0,subQ10,subQ11])],"isStart":true})});}
            var sketch = newSketch(context, id + "F16", { "sketchPlane" : qUnion([Q0])});
            skLineSegment(sketch, "E79", {"start": v(-33.56, 74.25) * mm, "end": v(-21.83, 87.9) * mm});
            skLineSegment(sketch, "E80", {"start": v(18.14, 74.25) * mm, "end": v(6.4, 87.9) * mm});
            skLineSegment(sketch, "E81", {"start": v(-21.83, 87.9) * mm, "end": v(-21.83, 99.9) * mm});
            skLineSegment(sketch, "E82", {"start": v(6.4, 87.9) * mm, "end": v(6.4, 99.9) * mm});
            skArc(sketch, "E83", {"start": v(6.4, 99.9) * mm, "mid": v(-7.7, 109.84) * mm, "end": v(-21.83, 99.9) * mm});
            skCircle(sketch, "E84", {"center": v(-7.7, 94.84) * mm, "radius": 6 * mm});
            skLineSegment(sketch, "E85", {"start": v(-74.25, 0) * mm, "end": v(74.25, 0) * mm, "construction": true});
            skLineSegment(sketch, "E86.MirrorCS", {"start": v(-33.56, -74.25) * mm, "end": v(-21.83, -87.9) * mm});
            skArc(sketch, "E87.MirrorCS", {"start": v(6.4, -99.9) * mm, "mid": v(-7.7, -109.84) * mm, "end": v(-21.83, -99.9) * mm});
            skCircle(sketch, "E88.MirrorC", {"center": v(-7.7, -94.84) * mm, "radius": 6 * mm});
            skLineSegment(sketch, "E89.MirrorCS", {"start": v(6.4, -87.9) * mm, "end": v(6.4, -99.9) * mm});
            skLineSegment(sketch, "E90.MirrorCS", {"start": v(-21.83, -87.9) * mm, "end": v(-21.83, -99.9) * mm});
            skLineSegment(sketch, "E91.MirrorCS", {"start": v(18.14, -74.25) * mm, "end": v(6.4, -87.9) * mm});
            skSolve(sketch);
        }
        {
            var Q0;
            {var subQ0=sQuery(id+"F16.wireOp",EDGE,"E79");Q0=makeQuery(id+"F16.imprint","IMPRINT",FACE,{"disambiguationData":[TD([[makeQuery(id+"F16.imprint","IMPRINT",EDGE,{"derivedFrom":subQ0}),-1.0]])]});}
            var Q1;
            Q1=makeQuery(id+"F16.imprint","IMPRINT",FACE,{"disambiguationData":[TD([[makeQuery(id+"F16.imprint","IMPRINT",EDGE,{"derivedFrom":makeQuery(id+"F1.opExtrude","CAP_EDGE",EDGE,{"disambiguationData":[OSD([sQuery(id+"F0.wireOp",EDGE,"E1.left")])],"isStart":true})}),-1.0]])]});
            var Q2;
            {var subQ0=sQuery(id+"F16.wireOp",EDGE,"E86.MirrorCS");Q2=makeQuery(id+"F16.imprint","IMPRINT",FACE,{"disambiguationData":[TD([[makeQuery(id+"F16.imprint","IMPRINT",EDGE,{"derivedFrom":subQ0}),1.0]])]});}
            extrude(context, id + "F17", {"entities" : qUnion([Q0, Q1, Q2]), "oppositeDirection" : true, "depth" : 3 * mm});
        }
    });
